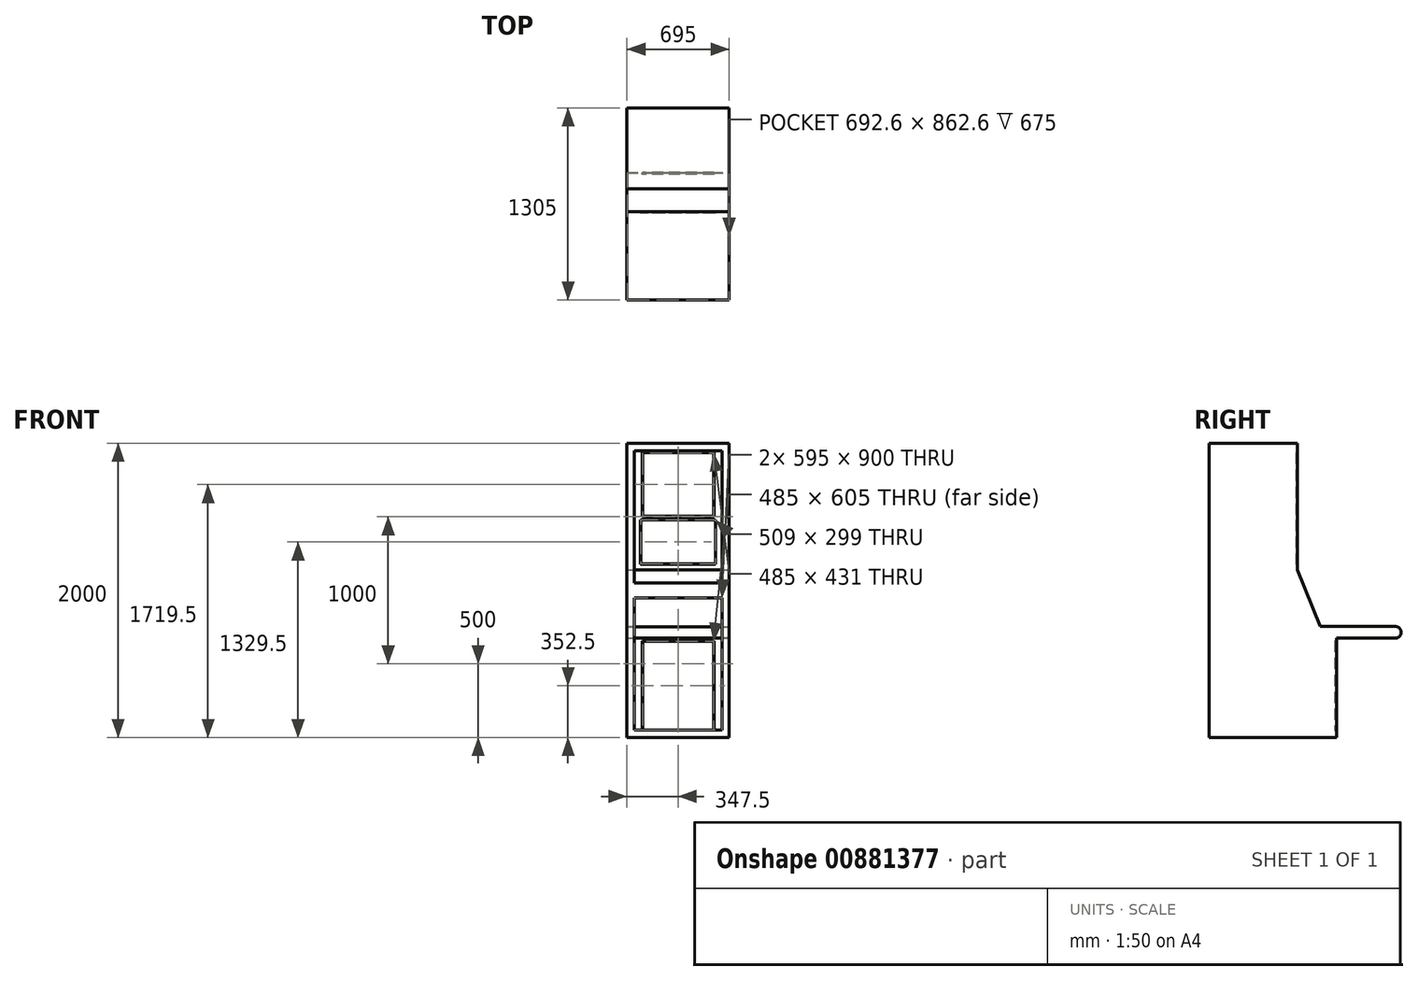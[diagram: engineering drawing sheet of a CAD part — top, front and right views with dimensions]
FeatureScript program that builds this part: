
annotation { "Feature Type Name" : "Feature", "Feature Type Description" : "" }
export const myFeature = defineFeature(function(context is Context, id is Id, definition is map)
    precondition{}
    {
        {
            var Q0;
            Q0=qCreatedBy(makeId("Right.planeOp"),FACE);
            var sketch = newSketch(context, id + "F0", { "sketchPlane" : qUnion([Q0])});
            skLineSegment(sketch, "E0", {"start": v(0, 0) * mm, "end": v(865, 0) * mm});
            skLineSegment(sketch, "E1", {"start": v(865, 0) * mm, "end": v(865, 675) * mm});
            skLineSegment(sketch, "E2", {"start": v(865, 675) * mm, "end": v(1265, 675) * mm});
            skLineSegment(sketch, "E3", {"start": v(1265, 675) * mm, "end": v(1265, 755) * mm, "construction": true});
            skLineSegment(sketch, "E4", {"start": v(1265, 755) * mm, "end": v(755.55, 755) * mm});
            skLineSegment(sketch, "E5", {"start": v(755.55, 755) * mm, "end": v(600, 1140) * mm});
            skLineSegment(sketch, "E6", {"start": v(600, 1140) * mm, "end": v(600, 2000) * mm});
            skLineSegment(sketch, "E7", {"start": v(600, 2000) * mm, "end": v(0, 2000) * mm});
            skLineSegment(sketch, "E8", {"start": v(0, 2000) * mm, "end": v(0, 0) * mm});
            skArc(sketch, "E9", {"start": v(1265, 675) * mm, "mid": v(1305, 715) * mm, "end": v(1265, 755) * mm});
            skSolve(sketch);
        }
        {
            var Q0;
            Q0 = qSketchRegion(id + "F0", true);
            extrude(context, id + "F1", {"entities" : qUnion([Q0]), "oppositeDirection" : true, "depth" : 695 * mm, "offsetDistance" : 25 * mm});
        }
        {
            var Q0;
            Q0=makeQuery(id+"F1.opExtrude","SWEPT_FACE",FACE,{"disambiguationData":[OSD([sQuery(id+"F0.wireOp",EDGE,"E8")])]});
            var sketch = newSketch(context, id + "F2", { "sketchPlane" : qUnion([Q0])});
            skLineSegment(sketch, "E10", {"start": v(-347.5, 2000) * mm, "end": v(-347.5, 0) * mm, "construction": true});
            skLineSegment(sketch, "E11.bottom", {"start": v(-645, 1950) * mm, "end": v(-50, 1950) * mm});
            skLineSegment(sketch, "E11.top", {"start": v(-645, 1050) * mm, "end": v(-50, 1050) * mm});
            skLineSegment(sketch, "E11.left", {"start": v(-645, 1950) * mm, "end": v(-645, 1050) * mm});
            skLineSegment(sketch, "E11.right", {"start": v(-50, 1950) * mm, "end": v(-50, 1050) * mm});
            skLineSegment(sketch, "E12.bottom", {"start": v(-645, 950) * mm, "end": v(-50, 950) * mm});
            skLineSegment(sketch, "E12.top", {"start": v(-645, 50) * mm, "end": v(-50, 50) * mm});
            skLineSegment(sketch, "E12.left", {"start": v(-645, 950) * mm, "end": v(-645, 50) * mm});
            skLineSegment(sketch, "E12.right", {"start": v(-50, 950) * mm, "end": v(-50, 50) * mm});
            skSolve(sketch);
        }
        {
            var Q0;
            Q0 = qSketchRegion(id + "F2", true);
            extrude(context, id + "F3", {"entities" : qUnion([Q0]), "operationType" : NewBodyOperationType.REMOVE, "oppositeDirection" : true, "depth" : 1.2 * mm, "offsetDistance" : 25 * mm});
        }
        {
            var Q0;
            Q0=makeQuery(id+"F1.opExtrude","SWEPT_FACE",FACE,{"disambiguationData":[OSD([sQuery(id+"F0.wireOp",EDGE,"E6")])]});
            var sketch = newSketch(context, id + "F4", { "sketchPlane" : qUnion([Q0])});
            skLineSegment(sketch, "E13", {"start": v(347.5, 2000) * mm, "end": v(347.5, 1140) * mm, "construction": true});
            skLineSegment(sketch, "E14.bottom", {"start": v(115, 1935) * mm, "end": v(580, 1935) * mm});
            skLineSegment(sketch, "E14.top", {"start": v(115, 1504) * mm, "end": v(580, 1504) * mm});
            skLineSegment(sketch, "E14.left", {"start": v(115, 1935) * mm, "end": v(115, 1504) * mm});
            skLineSegment(sketch, "E14.right", {"start": v(580, 1935) * mm, "end": v(580, 1504) * mm});
            skLineSegment(sketch, "E15.bottom", {"start": v(93, 1479) * mm, "end": v(602, 1479) * mm});
            skLineSegment(sketch, "E15.top", {"start": v(93, 1180) * mm, "end": v(602, 1180) * mm});
            skLineSegment(sketch, "E15.left", {"start": v(93, 1479) * mm, "end": v(93, 1180) * mm});
            skLineSegment(sketch, "E15.right", {"start": v(602, 1479) * mm, "end": v(602, 1180) * mm});
            skLineSegment(sketch, "E16.0", {"start": v(105, 1935) * mm, "end": v(105, 1504) * mm});
            skLineSegment(sketch, "E17.0", {"start": v(590, 1935) * mm, "end": v(590, 1504) * mm});
            skLineSegment(sketch, "E18", {"start": v(105, 1935) * mm, "end": v(115, 1935) * mm});
            skLineSegment(sketch, "E19", {"start": v(580, 1935) * mm, "end": v(590, 1935) * mm});
            skLineSegment(sketch, "E20", {"start": v(580, 1504) * mm, "end": v(590, 1504) * mm});
            skLineSegment(sketch, "E21", {"start": v(105, 1504) * mm, "end": v(115, 1504) * mm});
            skSolve(sketch);
        }
        {
            var Q0;
            Q0=makeQuery(id+"F4.imprint","IMPRINT",FACE,{"disambiguationData":[TD([[makeQuery(id+"F4.imprint","IMPRINT",EDGE,{"derivedFrom":sQuery(id+"F4.wireOp",EDGE,"E15.bottom")}),-1.0]])]});
            extrude(context, id + "F5", {"entities" : qUnion([Q0]), "operationType" : NewBodyOperationType.REMOVE, "oppositeDirection" : true, "depth" : 10 * mm, "offsetDistance" : 25 * mm});
        }
        {
            var Q0;
            Q0=makeQuery(id+"F4.imprint","IMPRINT",FACE,{"disambiguationData":[TD([[makeQuery(id+"F4.imprint","IMPRINT",EDGE,{"derivedFrom":sQuery(id+"F4.wireOp",EDGE,"E14.bottom")}),-1.0]])]});
            var Q1;
            Q1=makeQuery(id+"F4.imprint","IMPRINT",FACE,{"disambiguationData":[TD([[makeQuery(id+"F4.imprint","IMPRINT",EDGE,{"derivedFrom":sQuery(id+"F4.wireOp",EDGE,"E14.left")}),-1.0]])]});
            var Q2;
            Q2=makeQuery(id+"F4.imprint","IMPRINT",FACE,{"disambiguationData":[TD([[makeQuery(id+"F4.imprint","IMPRINT",EDGE,{"derivedFrom":sQuery(id+"F4.wireOp",EDGE,"E14.right")}),1.0]])]});
            extrude(context, id + "F6", {"entities" : qUnion([Q0, Q1, Q2]), "operationType" : NewBodyOperationType.REMOVE, "oppositeDirection" : true, "depth" : 10 * mm, "offsetDistance" : 25 * mm});
        }
        {
            var Q0;
            Q0=makeQuery(id+"F1.opExtrude","SWEPT_FACE",FACE,{"disambiguationData":[OSD([sQuery(id+"F0.wireOp",EDGE,"E1")])]});
            var sketch = newSketch(context, id + "F7", { "sketchPlane" : qUnion([Q0])});
            skLineSegment(sketch, "E22.bottom", {"start": v(105, 655) * mm, "end": v(590, 655) * mm});
            skLineSegment(sketch, "E22.top", {"start": v(105, 50) * mm, "end": v(590, 50) * mm});
            skLineSegment(sketch, "E22.left", {"start": v(105, 655) * mm, "end": v(105, 50) * mm});
            skLineSegment(sketch, "E22.right", {"start": v(590, 655) * mm, "end": v(590, 50) * mm});
            skLineSegment(sketch, "E23", {"start": v(115, 655) * mm, "end": v(115, 50) * mm});
            skLineSegment(sketch, "E24", {"start": v(580, 655) * mm, "end": v(580, 50) * mm});
            skSolve(sketch);
        }
        {
            var Q0;
            {var subQ0=sQuery(id+"F7.wireOp",EDGE,"E23");Q0=makeQuery(id+"F7.imprint","IMPRINT",FACE,{"disambiguationData":[TD([[makeQuery(id+"F7.imprint","IMPRINT",EDGE,{"derivedFrom":subQ0}),1.0]])]});}
            var Q1;
            {var subQ0=sQuery(id+"F7.wireOp",EDGE,"E22.left");Q1=makeQuery(id+"F7.imprint","IMPRINT",FACE,{"disambiguationData":[TD([[makeQuery(id+"F7.imprint","IMPRINT",EDGE,{"derivedFrom":subQ0}),1.0]])]});}
            var Q2;
            {var subQ0=sQuery(id+"F7.wireOp",EDGE,"E22.right");Q2=makeQuery(id+"F7.imprint","IMPRINT",FACE,{"disambiguationData":[TD([[makeQuery(id+"F7.imprint","IMPRINT",EDGE,{"derivedFrom":subQ0}),-1.0]])]});}
            extrude(context, id + "F8", {"entities" : qUnion([Q0, Q1, Q2]), "operationType" : NewBodyOperationType.REMOVE, "oppositeDirection" : true, "depth" : 10 * mm, "offsetDistance" : 25 * mm});
        }
        {
            var Q0;
            Q0=makeQuery(id+"F6.boolean.opBoolean","COPY",FACE,{"derivedFrom":makeQuery(id+"F6.opExtrude","CAP_FACE",FACE,{"disambiguationData":[OSD([sQuery(id+"F4.wireOp",EDGE,"E14.bottom"),sQuery(id+"F4.wireOp",EDGE,"E14.top"),sQuery(id+"F4.wireOp",EDGE,"E16.0"),sQuery(id+"F4.wireOp",EDGE,"E17.0"),sQuery(id+"F4.wireOp",EDGE,"E18"),sQuery(id+"F4.wireOp",EDGE,"E19"),sQuery(id+"F4.wireOp",EDGE,"E20"),sQuery(id+"F4.wireOp",EDGE,"E21")])],"isStart":false})});
            var Q1;
            Q1=makeQuery(id+"F5.boolean.opBoolean","COPY",FACE,{"derivedFrom":makeQuery(id+"F5.opExtrude","CAP_FACE",FACE,{"disambiguationData":[OSD([sQuery(id+"F4.wireOp",EDGE,"E15.bottom"),sQuery(id+"F4.wireOp",EDGE,"E15.top"),sQuery(id+"F4.wireOp",EDGE,"E15.left"),sQuery(id+"F4.wireOp",EDGE,"E15.right")])],"isStart":false})});
            var Q2;
            Q2=makeQuery(id+"F8.boolean.opBoolean","COPY",FACE,{"derivedFrom":makeQuery(id+"F8.opExtrude","CAP_FACE",FACE,{"disambiguationData":[OSD([sQuery(id+"F7.wireOp",EDGE,"E22.bottom"),sQuery(id+"F7.wireOp",EDGE,"E22.top"),sQuery(id+"F7.wireOp",EDGE,"E22.left"),sQuery(id+"F7.wireOp",EDGE,"E22.right")])],"isStart":false})});
            var Q3;
            Q3=makeQuery(id+"F3.boolean.opBoolean","COPY",FACE,{"derivedFrom":makeQuery(id+"F3.opExtrude","CAP_FACE",FACE,{"disambiguationData":[OSD([sQuery(id+"F2.wireOp",EDGE,"E12.bottom"),sQuery(id+"F2.wireOp",EDGE,"E12.top"),sQuery(id+"F2.wireOp",EDGE,"E12.left"),sQuery(id+"F2.wireOp",EDGE,"E12.right")])],"isStart":false})});
            var Q4;
            Q4=makeQuery(id+"F3.boolean.opBoolean","COPY",FACE,{"derivedFrom":makeQuery(id+"F3.opExtrude","CAP_FACE",FACE,{"disambiguationData":[OSD([sQuery(id+"F2.wireOp",EDGE,"E11.bottom"),sQuery(id+"F2.wireOp",EDGE,"E11.top"),sQuery(id+"F2.wireOp",EDGE,"E11.left"),sQuery(id+"F2.wireOp",EDGE,"E11.right")])],"isStart":false})});
            shell(context, id + "F9", {"entities" : qUnion([Q0, Q1, Q2, Q3, Q4]), "thickness" : 1.2 * mm});
        }
    });
